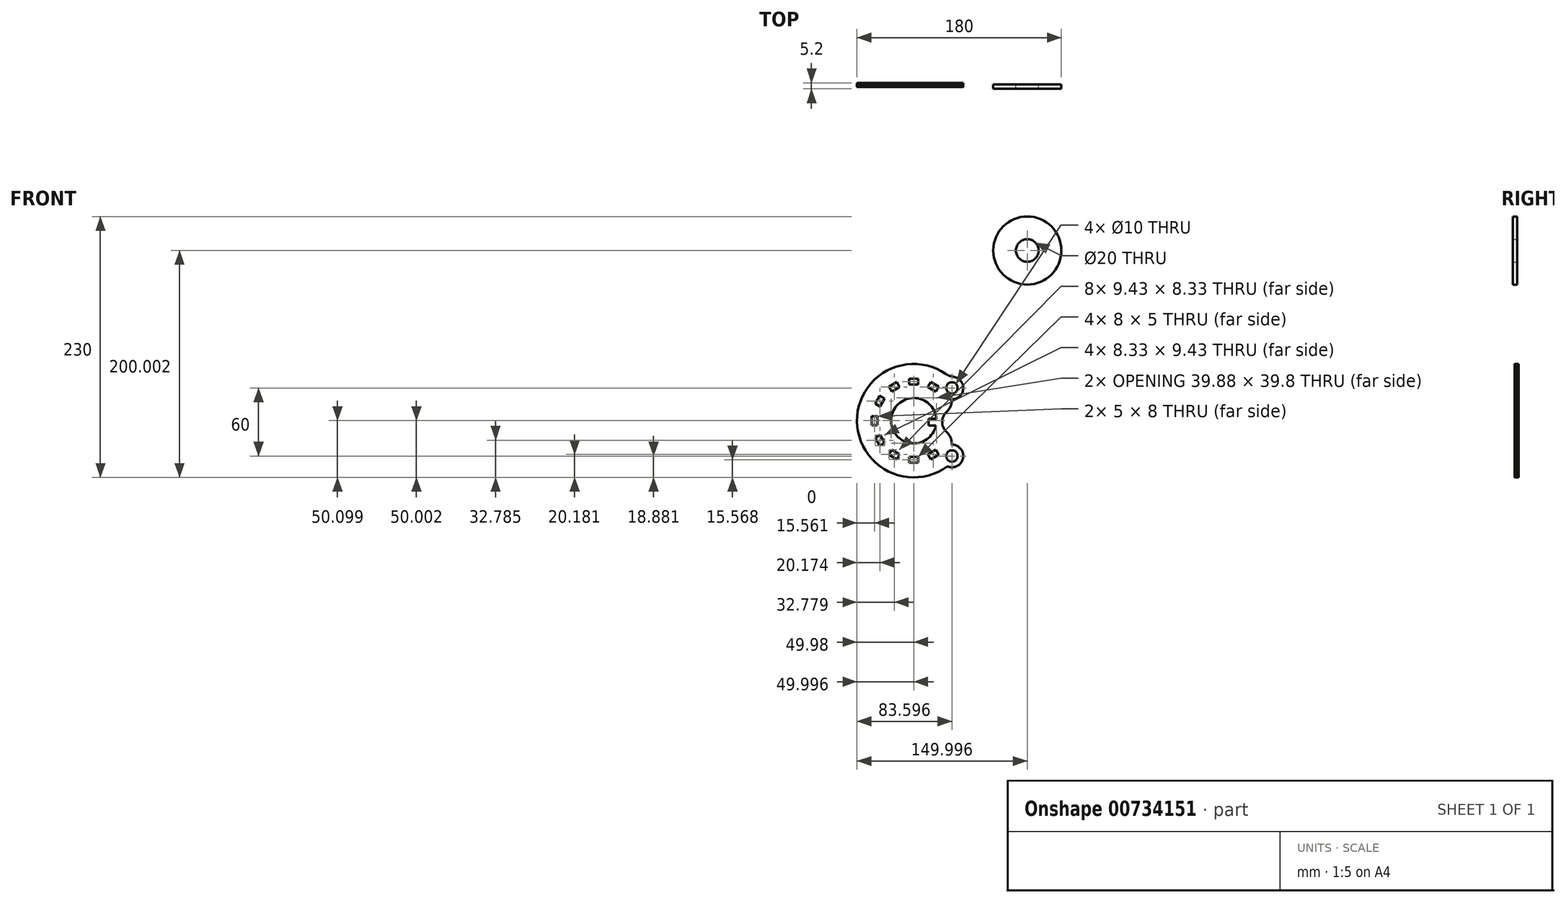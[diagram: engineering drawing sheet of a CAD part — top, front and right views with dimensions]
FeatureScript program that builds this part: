
annotation { "Feature Type Name" : "Feature", "Feature Type Description" : "" }
export const myFeature = defineFeature(function(context is Context, id is Id, definition is map)
    precondition{}
    {
        {
            var Q0;
            Q0=qCreatedBy(makeId("Front.planeOp"),FACE);
            var sketch = newSketch(context, id + "F0", { "sketchPlane" : qUnion([Q0])});
            skCircle(sketch, "E0", {"center": v(67.17, 111.12) * mm, "radius": 30 * mm});
            skCircle(sketch, "E1.0", {"center": v(67.17, 111.12) * mm, "radius": 10 * mm});
            skArc(sketch, "E2", {"start": v(-12.9, -37.15) * mm, "mid": v(-52.8, -37.59) * mm, "end": v(-13.3, -43.15) * mm});
            skLineSegment(sketch, "E3", {"start": v(-12.9, -37.15) * mm, "end": v(-19.9, -37.15) * mm});
            skLineSegment(sketch, "E4", {"start": v(-13.3, -43.15) * mm, "end": v(-19.9, -43.15) * mm});
            skLineSegment(sketch, "E5", {"start": v(-19.9, -43.15) * mm, "end": v(-19.9, -37.15) * mm});
            skArc(sketch, "E6", {"start": v(-4.5, 2.32) * mm, "mid": v(-82.83, -39.53) * mm, "end": v(-3.44, -79.33) * mm});
            skCircle(sketch, "E7", {"center": v(0.77, -10) * mm, "radius": 5 * mm});
            skCircle(sketch, "E8", {"center": v(0.77, -70) * mm, "radius": 5 * mm});
            skLineSegment(sketch, "E9.bottom", {"start": v(-36.83, -1.94) * mm, "end": v(-28.83, -1.94) * mm});
            skLineSegment(sketch, "E9.top", {"start": v(-36.83, -6.94) * mm, "end": v(-28.83, -6.94) * mm});
            skLineSegment(sketch, "E9.left", {"start": v(-36.83, -1.94) * mm, "end": v(-36.83, -6.94) * mm});
            skLineSegment(sketch, "E9.right", {"start": v(-28.83, -1.94) * mm, "end": v(-28.83, -6.94) * mm});
            skLineSegment(sketch, "E10.1.0", {"start": v(-54.77, -8.9) * mm, "end": v(-47.84, -4.9) * mm});
            skLineSegment(sketch, "E10.1.1", {"start": v(-47.84, -4.9) * mm, "end": v(-45.34, -9.22) * mm});
            skLineSegment(sketch, "E10.1.2", {"start": v(-52.27, -13.22) * mm, "end": v(-45.34, -9.22) * mm});
            skLineSegment(sketch, "E10.1.3", {"start": v(-54.77, -8.9) * mm, "end": v(-52.27, -13.22) * mm});
            skLineSegment(sketch, "E10.2.0", {"start": v(-66.82, -23.87) * mm, "end": v(-62.82, -16.95) * mm});
            skLineSegment(sketch, "E10.2.1", {"start": v(-62.82, -16.95) * mm, "end": v(-58.5, -19.45) * mm});
            skLineSegment(sketch, "E10.2.2", {"start": v(-62.5, -26.37) * mm, "end": v(-58.5, -19.45) * mm});
            skLineSegment(sketch, "E10.2.3", {"start": v(-66.82, -23.87) * mm, "end": v(-62.5, -26.37) * mm});
            skLineSegment(sketch, "E10.3.0", {"start": v(-69.77, -42.88) * mm, "end": v(-69.77, -34.88) * mm});
            skLineSegment(sketch, "E10.3.1", {"start": v(-69.77, -34.88) * mm, "end": v(-64.77, -34.88) * mm});
            skLineSegment(sketch, "E10.3.2", {"start": v(-64.77, -42.88) * mm, "end": v(-64.77, -34.88) * mm});
            skLineSegment(sketch, "E10.3.3", {"start": v(-69.77, -42.88) * mm, "end": v(-64.77, -42.88) * mm});
            skLineSegment(sketch, "E10.4.0", {"start": v(-62.82, -60.8) * mm, "end": v(-66.82, -53.88) * mm});
            skLineSegment(sketch, "E10.4.1", {"start": v(-66.82, -53.88) * mm, "end": v(-62.5, -51.38) * mm});
            skLineSegment(sketch, "E10.4.2", {"start": v(-58.5, -58.3) * mm, "end": v(-62.5, -51.38) * mm});
            skLineSegment(sketch, "E10.4.3", {"start": v(-62.82, -60.8) * mm, "end": v(-58.5, -58.3) * mm});
            skLineSegment(sketch, "E10.5.0", {"start": v(-47.84, -72.86) * mm, "end": v(-54.77, -68.86) * mm});
            skLineSegment(sketch, "E10.5.1", {"start": v(-54.77, -68.86) * mm, "end": v(-52.27, -64.53) * mm});
            skLineSegment(sketch, "E10.5.2", {"start": v(-45.34, -68.53) * mm, "end": v(-52.27, -64.53) * mm});
            skLineSegment(sketch, "E10.5.3", {"start": v(-47.84, -72.86) * mm, "end": v(-45.34, -68.53) * mm});
            skLineSegment(sketch, "E10.6.0", {"start": v(-28.83, -75.81) * mm, "end": v(-36.83, -75.81) * mm});
            skLineSegment(sketch, "E10.6.1", {"start": v(-36.83, -75.81) * mm, "end": v(-36.83, -70.81) * mm});
            skLineSegment(sketch, "E10.6.2", {"start": v(-28.83, -70.81) * mm, "end": v(-36.83, -70.81) * mm});
            skLineSegment(sketch, "E10.6.3", {"start": v(-28.83, -75.81) * mm, "end": v(-28.83, -70.81) * mm});
            skLineSegment(sketch, "E10.7.0", {"start": v(-10.9, -68.86) * mm, "end": v(-17.83, -72.86) * mm});
            skLineSegment(sketch, "E10.7.1", {"start": v(-17.83, -72.86) * mm, "end": v(-20.33, -68.53) * mm});
            skLineSegment(sketch, "E10.7.2", {"start": v(-13.4, -64.53) * mm, "end": v(-20.33, -68.53) * mm});
            skLineSegment(sketch, "E10.7.3", {"start": v(-10.9, -68.86) * mm, "end": v(-13.4, -64.53) * mm});
            skLineSegment(sketch, "E10.11.0", {"start": v(-17.83, -4.9) * mm, "end": v(-10.9, -8.9) * mm});
            skLineSegment(sketch, "E10.11.1", {"start": v(-10.9, -8.9) * mm, "end": v(-13.4, -13.22) * mm});
            skLineSegment(sketch, "E10.11.2", {"start": v(-20.33, -9.22) * mm, "end": v(-13.4, -13.22) * mm});
            skLineSegment(sketch, "E10.11.3", {"start": v(-17.83, -4.9) * mm, "end": v(-20.33, -9.22) * mm});
            skArc(sketch, "E11", {"start": v(0.91, 0) * mm, "mid": v(10.77, -10.07) * mm, "end": v(0.77, -20) * mm});
            skArc(sketch, "E12", {"start": v(0.77, -60) * mm, "mid": v(10.56, -72.04) * mm, "end": v(-3.22, -79.17) * mm});
            skArc(sketch, "E13", {"start": v(-4.5, 2.32) * mm, "mid": v(-1.9, 0.9) * mm, "end": v(0.91, 0) * mm});
            skArc(sketch, "E14", {"start": v(-3.22, -79.17) * mm, "mid": v(-3.33, -79.25) * mm, "end": v(-3.44, -79.33) * mm});
            skArc(sketch, "E15", {"start": v(-4.01, -31.22) * mm, "mid": v(-7.83, -40) * mm, "end": v(-4.01, -48.78) * mm});
            skArc(sketch, "E16", {"start": v(-4.01, -31.22) * mm, "mid": v(-0.43, -26.11) * mm, "end": v(0.77, -20) * mm});
            skArc(sketch, "E17", {"start": v(0.77, -60) * mm, "mid": v(-0.43, -53.88) * mm, "end": v(-4.01, -48.78) * mm});
            skArc(sketch, "E18", {"start": v(-56.23, 5.3) * mm, "mid": v(0.11, 49.7) * mm, "end": v(37.17, 111.12) * mm});
            skArc(sketch, "E19", {"start": v(7.02, -77.8) * mm, "mid": v(72.37, 3.83) * mm, "end": v(96.64, 105.55) * mm});
            skSolve(sketch);
        }
        {
            var Q0;
            Q0=makeQuery(id+"F0.imprint","IMPRINT",FACE,{"disambiguationData":[TD([[makeQuery(id+"F0.imprint","IMPRINT",EDGE,{"derivedFrom":sQuery(id+"F0.wireOp",EDGE,"E2")}),-1.0]])]});
            extrude(context, id + "F1", {"entities" : qUnion([Q0]), "depth" : 2.3 * mm, "offsetDistance" : 25 * mm});
        }
        {
            var Q0;
            Q0=makeQuery(id+"F0.imprint","IMPRINT",FACE,{"disambiguationData":[TD([[makeQuery(id+"F0.imprint","IMPRINT",EDGE,{"derivedFrom":sQuery(id+"F0.wireOp",EDGE,"E1.0")}),-1.0]])]});
            extrude(context, id + "F2", {"entities" : qUnion([Q0]), "depth" : 4 * mm, "offsetDistance" : 25 * mm});
        }
        {
            var Q0;
            Q0=makeQuery(id+"F0.imprint","IMPRINT",FACE,{"disambiguationData":[TD([[makeQuery(id+"F0.imprint","IMPRINT",EDGE,{"derivedFrom":sQuery(id+"F0.wireOp",EDGE,"E11")}),1.0]])]});
            extrude(context, id + "F3", {"entities" : qUnion([Q0]), "endBound" : BoundingType.SYMMETRIC, "depth" : 2.4 * mm, "offsetDistance" : 25 * mm});
        }
        {
            var Q0;
            Q0=makeQuery(id+"F1.opExtrude","CAP_EDGE",EDGE,{"disambiguationData":[OSD([sQuery(id+"F0.wireOp",EDGE,"E13")])],"isStart":false});
            var Q1;
            Q1=makeQuery(id+"F1.opExtrude","CAP_EDGE",EDGE,{"disambiguationData":[OSD([sQuery(id+"F0.wireOp",EDGE,"E11")])],"isStart":false});
            var Q2;
            Q2=makeQuery(id+"F1.opExtrude","CAP_EDGE",EDGE,{"disambiguationData":[OSD([sQuery(id+"F0.wireOp",EDGE,"E17")])],"isStart":false});
            var Q3;
            Q3=makeQuery(id+"F1.opExtrude","CAP_EDGE",EDGE,{"disambiguationData":[OSD([sQuery(id+"F0.wireOp",EDGE,"E12")])],"isStart":false});
            fillet(context, id + "F4", {"entities" : qUnion([Q0, Q1, Q2, Q3]), "radius" : .25 * mm, "tangentPropagation" : true, "allowEdgeOverflow" : false});
        }
    });
